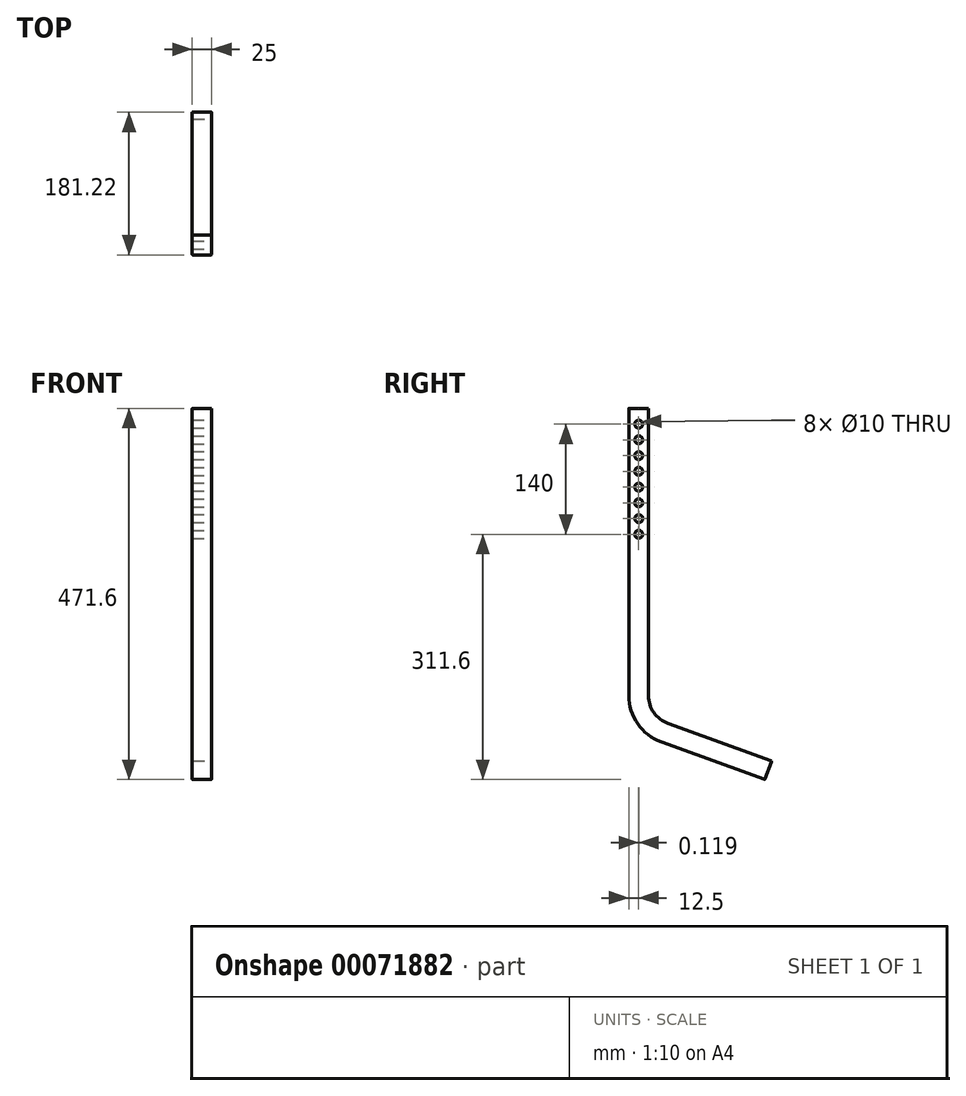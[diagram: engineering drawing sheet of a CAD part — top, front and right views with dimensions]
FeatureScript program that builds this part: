
annotation { "Feature Type Name" : "Feature", "Feature Type Description" : "" }
export const myFeature = defineFeature(function(context is Context, id is Id, definition is map)
    precondition{}
    {
        {
            var Q0;
            Q0=qCreatedBy(makeId("Top.planeOp"),FACE);
            var sketch = newSketch(context, id + "F0", { "sketchPlane" : qUnion([Q0])});
            skPoint(sketch, "E0.middle", {"position": v(0, 0) * mm});
            skLineSegment(sketch, "E1.bottom", {"start": v(-12.5, -12.5) * mm, "end": v(12.5, -12.5) * mm});
            skLineSegment(sketch, "E1.top", {"start": v(-12.5, 12.5) * mm, "end": v(12.5, 12.5) * mm});
            skLineSegment(sketch, "E1.left", {"start": v(-12.5, -12.5) * mm, "end": v(-12.5, 12.5) * mm});
            skLineSegment(sketch, "E1.right", {"start": v(12.5, -12.5) * mm, "end": v(12.5, 12.5) * mm});
            skSolve(sketch);
        }
        {
            var Q0;
            Q0=qCreatedBy(makeId("Right.planeOp"),FACE);
            var sketch = newSketch(context, id + "F1", { "sketchPlane" : qUnion([Q0])});
            skLineSegment(sketch, "E2", {"start": v(0, 0) * mm, "end": v(0, -364.99) * mm});
            skLineSegment(sketch, "E3", {"start": v(32.9, -411.97) * mm, "end": v(164.45, -459.85) * mm});
            skPoint(sketch, "E4.visualSharp", {"position": v(0, -400) * mm});
            skArc(sketch, "E4.filletArc", {"start": v(0, -364.99) * mm, "mid": v(9.04, -393.67) * mm, "end": v(32.9, -411.97) * mm});
            skSolve(sketch);
        }
        {
            var Q0;
            Q0 = qSketchRegion(id + "F0", true);
            var Q1;
            Q1 = qConstructionFilter(qBodyType(qCreatedBy(id + "F1" ,EDGE), BodyType.WIRE), ConstructionObject.NO);
            sweep(context, id + "F2", {"profiles" : qUnion([Q0]), "path" : qUnion([Q1])});
        }
        {
            var Q0;
            Q0=makeQuery(id+"F2.opSweep","SWEPT_EDGE",EDGE,{"disambiguationData":[OSD([sQuery(id+"F0.wireOp",EDGE,"E1.bottom"),sQuery(id+"F0.wireOp",EDGE,"E1.right"),sQuery(id+"F1.wireOp",EDGE,"E2")])]});
            var Q1;
            Q1=makeQuery(id+"F2.opSweep","SWEPT_EDGE",EDGE,{"disambiguationData":[OSD([sQuery(id+"F0.wireOp",EDGE,"E1.bottom"),sQuery(id+"F0.wireOp",EDGE,"E1.right"),sQuery(id+"F1.wireOp",EDGE,"E4.filletArc")])]});
            var Q2;
            Q2=makeQuery(id+"F2.opSweep","SWEPT_EDGE",EDGE,{"disambiguationData":[OSD([sQuery(id+"F0.wireOp",EDGE,"E1.bottom"),sQuery(id+"F0.wireOp",EDGE,"E1.left"),sQuery(id+"F1.wireOp",EDGE,"E3")])]});
            var Q3;
            Q3=makeQuery(id+"F2.opSweep","SWEPT_EDGE",EDGE,{"disambiguationData":[OSD([sQuery(id+"F0.wireOp",EDGE,"E1.top"),sQuery(id+"F0.wireOp",EDGE,"E1.right"),sQuery(id+"F1.wireOp",EDGE,"E3")])]});
            var Q4;
            Q4=makeQuery(id+"F2.opSweep","SWEPT_EDGE",EDGE,{"disambiguationData":[OSD([sQuery(id+"F0.wireOp",EDGE,"E1.top"),sQuery(id+"F0.wireOp",EDGE,"E1.left"),sQuery(id+"F1.wireOp",EDGE,"E3")])]});
            fillet(context, id + "F3", {"entities" : qUnion([Q0, Q1, Q2, Q3, Q4]), "radius" : 1 * mm, "tangentPropagation" : true, "allowEdgeOverflow" : false});
        }
        {
            var Q0;
            Q0=qCreatedBy(makeId("Right.planeOp"),FACE);
            var sketch = newSketch(context, id + "F4", { "sketchPlane" : qUnion([Q0])});
            skCircle(sketch, "E5", {"center": v(0, -20) * mm, "radius": 5 * mm});
            skCircle(sketch, "E6", {"center": v(0, -40) * mm, "radius": 5 * mm});
            skCircle(sketch, "E7", {"center": v(0, -60) * mm, "radius": 5 * mm});
            skCircle(sketch, "E8", {"center": v(0, -80) * mm, "radius": 5 * mm});
            skCircle(sketch, "E9", {"center": v(0, -100) * mm, "radius": 5 * mm});
            skCircle(sketch, "E10", {"center": v(0, -120) * mm, "radius": 5 * mm});
            skCircle(sketch, "E11", {"center": v(0.12, -140) * mm, "radius": 5 * mm});
            skCircle(sketch, "E12", {"center": v(0, -160) * mm, "radius": 5 * mm});
            skSolve(sketch);
        }
        {
            var Q0;
            Q0 = qSketchRegion(id + "F4", true);
            extrude(context, id + "F5", {"entities" : qUnion([Q0]), "operationType" : NewBodyOperationType.REMOVE, "endBound" : BoundingType.THROUGH_ALL, "oppositeDirection" : true, "depth" : 25 * mm, "hasSecondDirection" : true, "secondDirectionBound" : SecondDirectionBoundingType.THROUGH_ALL, "secondDirectionOppositeDirection" : false, "secondDirectionDepth" : 25 * mm});
        }
    });
